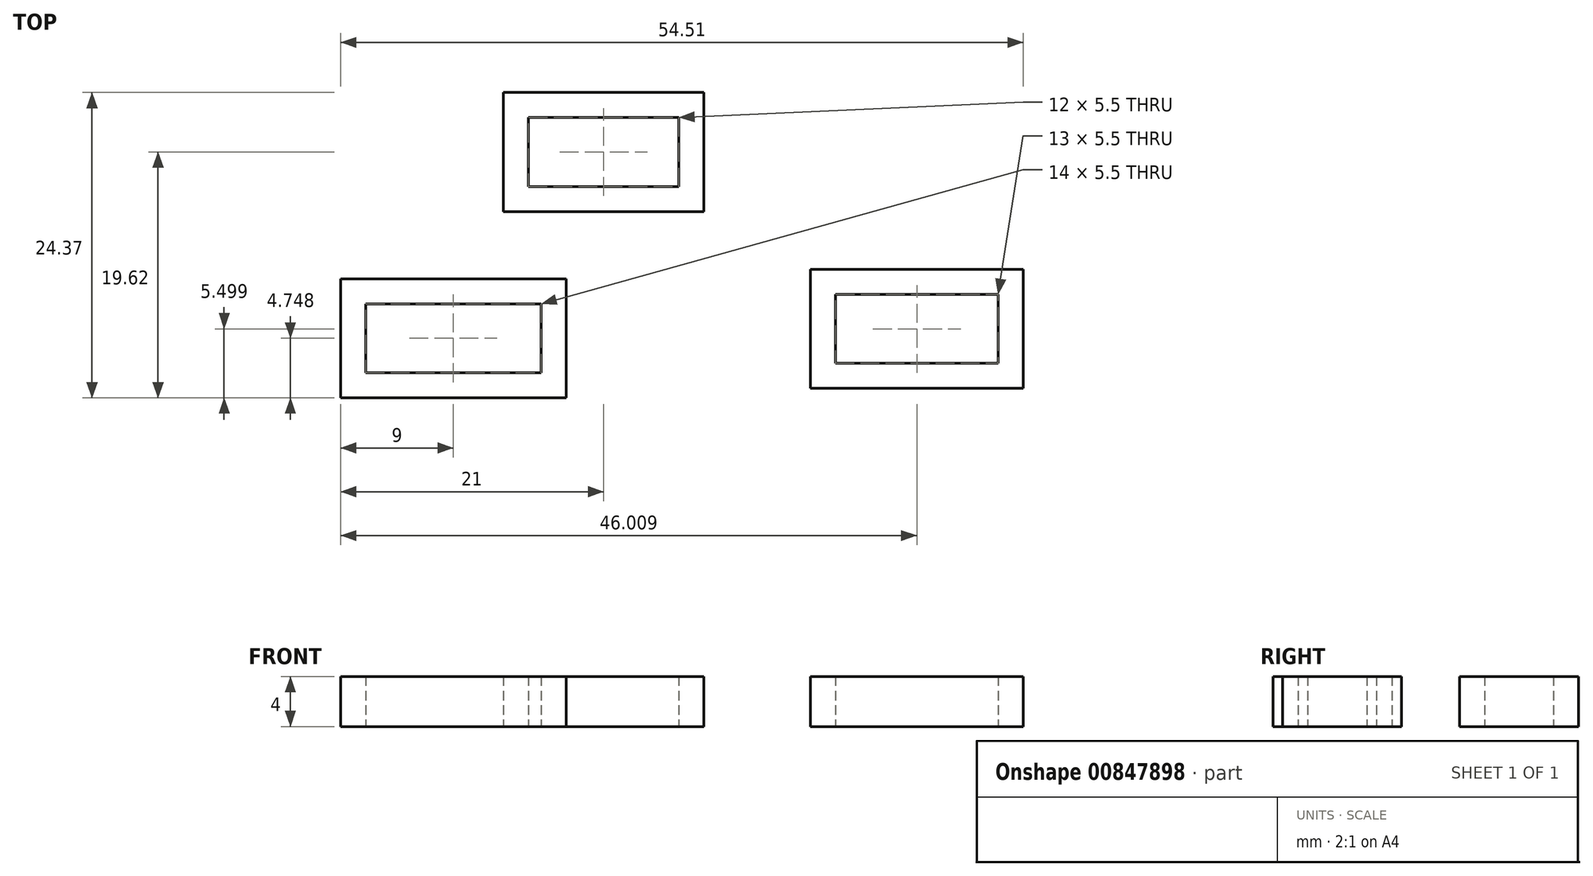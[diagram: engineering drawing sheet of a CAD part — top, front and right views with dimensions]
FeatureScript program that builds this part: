
annotation { "Feature Type Name" : "Feature", "Feature Type Description" : "" }
export const myFeature = defineFeature(function(context is Context, id is Id, definition is map)
    precondition{}
    {
        {
            var Q0;
            Q0=qCreatedBy(makeId("Top.planeOp"),FACE);
            var sketch = newSketch(context, id + "F0", { "sketchPlane" : qUnion([Q0])});
            skLineSegment(sketch, "E0.bottom", {"start": v(6, -2.75) * mm, "end": v(-6, -2.75) * mm});
            skLineSegment(sketch, "E0.top", {"start": v(6, 2.75) * mm, "end": v(-6, 2.75) * mm});
            skLineSegment(sketch, "E0.left", {"start": v(6, -2.75) * mm, "end": v(6, 2.75) * mm});
            skLineSegment(sketch, "E0.right", {"start": v(-6, -2.75) * mm, "end": v(-6, 2.75) * mm});
            skPoint(sketch, "E0.middle", {"position": v(0, 0) * mm});
            skLineSegment(sketch, "E1.bottom", {"start": v(8, -4.75) * mm, "end": v(-8, -4.75) * mm});
            skLineSegment(sketch, "E1.top", {"start": v(8, 4.75) * mm, "end": v(-8, 4.75) * mm});
            skLineSegment(sketch, "E1.left", {"start": v(8, -4.75) * mm, "end": v(8, 4.75) * mm});
            skLineSegment(sketch, "E1.right", {"start": v(-8, -4.75) * mm, "end": v(-8, 4.75) * mm});
            skLineSegment(sketch, "E2.bottom", {"start": v(31.5, -16.87) * mm, "end": v(18.5, -16.87) * mm});
            skLineSegment(sketch, "E2.top", {"start": v(31.5, -11.37) * mm, "end": v(18.5, -11.37) * mm});
            skLineSegment(sketch, "E2.left", {"start": v(31.5, -16.87) * mm, "end": v(31.5, -11.37) * mm});
            skLineSegment(sketch, "E2.right", {"start": v(18.5, -16.87) * mm, "end": v(18.5, -11.37) * mm});
            skPoint(sketch, "E2.middle", {"position": v(25, -14.12) * mm});
            skLineSegment(sketch, "E3.bottom", {"start": v(33.5, -18.87) * mm, "end": v(16.5, -18.87) * mm});
            skLineSegment(sketch, "E3.top", {"start": v(33.5, -9.37) * mm, "end": v(16.5, -9.37) * mm});
            skLineSegment(sketch, "E3.left", {"start": v(33.5, -18.87) * mm, "end": v(33.5, -9.37) * mm});
            skLineSegment(sketch, "E3.right", {"start": v(16.5, -18.87) * mm, "end": v(16.5, -9.37) * mm});
            skLineSegment(sketch, "E4.bottom", {"start": v(-5, -17.62) * mm, "end": v(-19, -17.62) * mm});
            skLineSegment(sketch, "E4.top", {"start": v(-5, -12.12) * mm, "end": v(-19, -12.12) * mm});
            skLineSegment(sketch, "E4.left", {"start": v(-5, -17.62) * mm, "end": v(-5, -12.12) * mm});
            skLineSegment(sketch, "E4.right", {"start": v(-19, -17.62) * mm, "end": v(-19, -12.12) * mm});
            skPoint(sketch, "E4.middle", {"position": v(-12, -14.87) * mm});
            skLineSegment(sketch, "E5.bottom", {"start": v(-3, -19.62) * mm, "end": v(-21, -19.62) * mm});
            skLineSegment(sketch, "E5.top", {"start": v(-3, -10.12) * mm, "end": v(-21, -10.12) * mm});
            skLineSegment(sketch, "E5.left", {"start": v(-3, -19.62) * mm, "end": v(-3, -10.12) * mm});
            skLineSegment(sketch, "E5.right", {"start": v(-21, -19.62) * mm, "end": v(-21, -10.12) * mm});
            skSolve(sketch);
        }
        {
            var Q0;
            Q0=makeQuery(id+"F0.imprint","IMPRINT",FACE,{"disambiguationData":[TD([[makeQuery(id+"F0.imprint","IMPRINT",EDGE,{"derivedFrom":sQuery(id+"F0.wireOp",EDGE,"E4.bottom")}),1.0]])]});
            var Q1;
            Q1=makeQuery(id+"F0.imprint","IMPRINT",FACE,{"disambiguationData":[TD([[makeQuery(id+"F0.imprint","IMPRINT",EDGE,{"derivedFrom":sQuery(id+"F0.wireOp",EDGE,"E0.bottom")}),1.0]])]});
            var Q2;
            Q2=makeQuery(id+"F0.imprint","IMPRINT",FACE,{"disambiguationData":[TD([[makeQuery(id+"F0.imprint","IMPRINT",EDGE,{"derivedFrom":sQuery(id+"F0.wireOp",EDGE,"E2.bottom")}),1.0]])]});
            extrude(context, id + "F1", {"entities" : qUnion([Q0, Q1, Q2]), "depth" : 4 * mm, "offsetDistance" : 25 * mm});
        }
    });
